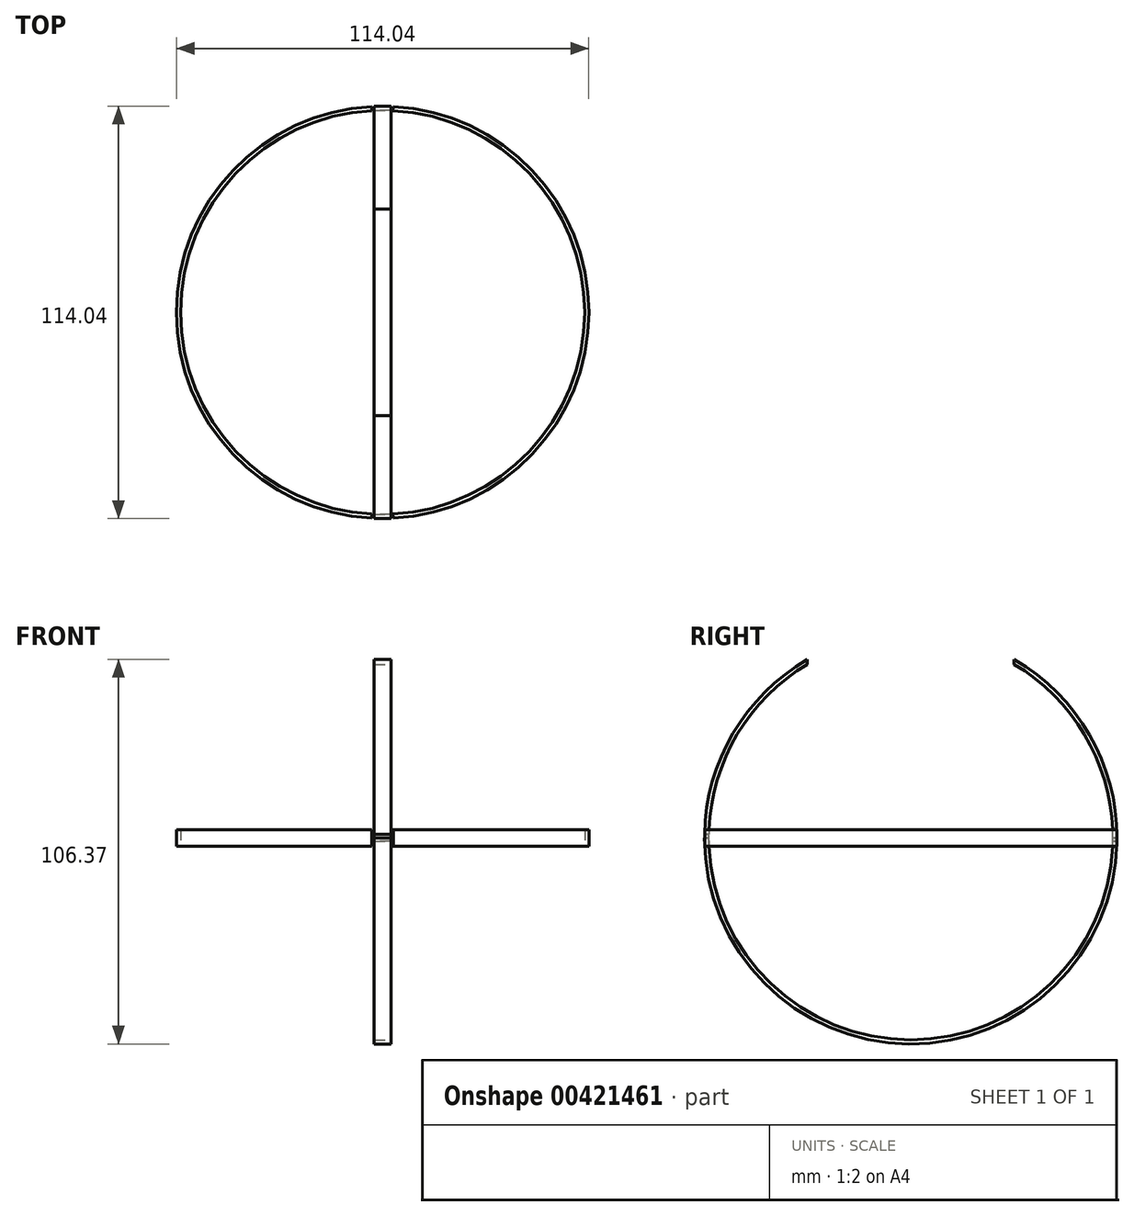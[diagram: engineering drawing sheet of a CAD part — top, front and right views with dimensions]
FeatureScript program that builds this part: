
annotation { "Feature Type Name" : "Feature", "Feature Type Description" : "" }
export const myFeature = defineFeature(function(context is Context, id is Id, definition is map)
    precondition{}
    {
        {
            var Q0;
            Q0=qCreatedBy(makeId("Front.planeOp"),FACE);
            var sketch = newSketch(context, id + "F0", { "sketchPlane" : qUnion([Q0])});
            skLineSegment(sketch, "E0", {"start": v(0, 0) * mm, "end": v(55.88, 0) * mm});
            skLineSegment(sketch, "E1", {"start": v(55.88, 0) * mm, "end": v(55.88, 2.29) * mm});
            skLineSegment(sketch, "E2", {"start": v(55.88, 2.29) * mm, "end": v(57.02, 2.29) * mm});
            skLineSegment(sketch, "E3", {"start": v(57.02, 2.29) * mm, "end": v(57.02, -2.29) * mm});
            skLineSegment(sketch, "E4", {"start": v(57.02, -2.29) * mm, "end": v(55.88, -2.29) * mm});
            skLineSegment(sketch, "E5", {"start": v(55.88, -2.29) * mm, "end": v(55.88, 0) * mm});
            skLineSegment(sketch, "E6", {"start": v(0, 0) * mm, "end": v(0, 55.88) * mm});
            skLineSegment(sketch, "E7", {"start": v(0, 55.88) * mm, "end": v(2.29, 55.88) * mm});
            skLineSegment(sketch, "E8", {"start": v(2.29, 55.88) * mm, "end": v(2.29, 57.02) * mm});
            skLineSegment(sketch, "E9", {"start": v(2.29, 57.02) * mm, "end": v(-2.29, 57.02) * mm});
            skLineSegment(sketch, "E10", {"start": v(-2.29, 57.02) * mm, "end": v(-2.29, 55.88) * mm});
            skLineSegment(sketch, "E11", {"start": v(0, 55.88) * mm, "end": v(-2.29, 55.88) * mm});
            skLineSegment(sketch, "E12.MirrorCS", {"start": v(-55.88, 0) * mm, "end": v(-55.88, 2.29) * mm});
            skLineSegment(sketch, "E13.MirrorCS", {"start": v(0, 0) * mm, "end": v(-55.88, 0) * mm});
            skLineSegment(sketch, "E14.MirrorCS", {"start": v(-55.88, -2.29) * mm, "end": v(-55.88, 0) * mm});
            skLineSegment(sketch, "E15.MirrorCS", {"start": v(-57.02, -2.29) * mm, "end": v(-55.88, -2.29) * mm});
            skLineSegment(sketch, "E16.MirrorCS", {"start": v(-57.02, 2.29) * mm, "end": v(-57.02, -2.29) * mm});
            skLineSegment(sketch, "E17.MirrorCS", {"start": v(-55.88, 2.29) * mm, "end": v(-57.02, 2.29) * mm});
            skLineSegment(sketch, "E18.MirrorCS", {"start": v(0, 0) * mm, "end": v(0, -55.88) * mm});
            skLineSegment(sketch, "E19.MirrorCS", {"start": v(2.29, -57.02) * mm, "end": v(-2.29, -57.02) * mm});
            skLineSegment(sketch, "E20.MirrorCS", {"start": v(-2.29, -57.02) * mm, "end": v(-2.29, -55.88) * mm});
            skLineSegment(sketch, "E21.MirrorCS", {"start": v(0, -55.88) * mm, "end": v(-2.29, -55.88) * mm});
            skLineSegment(sketch, "E22.MirrorCS", {"start": v(0, -55.88) * mm, "end": v(2.29, -55.88) * mm});
            skLineSegment(sketch, "E23.MirrorCS", {"start": v(2.29, -55.88) * mm, "end": v(2.29, -57.02) * mm});
            skSolve(sketch);
        }
        {
            var Q0;
            Q0=makeQuery(id+"F0.imprint","IMPRINT",FACE,{"disambiguationData":[TD([[makeQuery(id+"F0.imprint","IMPRINT",EDGE,{"derivedFrom":sQuery(id+"F0.wireOp",EDGE,"E19.MirrorCS")}),-1.0]])]});
            var Q1;
            Q1=makeQuery(id+"F0.imprint","IMPRINT",FACE,{"disambiguationData":[TD([[makeQuery(id+"F0.imprint","IMPRINT",EDGE,{"derivedFrom":sQuery(id+"F0.wireOp",EDGE,"E7")}),1.0]])]});
            var Q2;
            Q2=sQuery(id+"F0.wireOp",EDGE,"E13.MirrorCS");
            revolve(context, id + "F1", {"entities" : qUnion([Q0, Q1]), "axis" : qUnion([Q2]), "revolveType" : RevolveType.TWO_DIRECTIONS, "angle" : 90 * degree, "angleBack" : 271 * degree});
        }
        {
            var Q0;
            Q0=makeQuery(id+"F0.imprint","IMPRINT",FACE,{"disambiguationData":[TD([[makeQuery(id+"F0.imprint","IMPRINT",EDGE,{"derivedFrom":sQuery(id+"F0.wireOp",EDGE,"E12.MirrorCS")}),1.0]])]});
            var Q1;
            Q1=makeQuery(id+"F0.imprint","IMPRINT",FACE,{"disambiguationData":[TD([[makeQuery(id+"F0.imprint","IMPRINT",EDGE,{"derivedFrom":sQuery(id+"F0.wireOp",EDGE,"E1")}),-1.0]])]});
            var Q2;
            Q2=sQuery(id+"F0.wireOp",EDGE,"E6");
            revolve(context, id + "F2", {"entities" : qUnion([Q0, Q1]), "axis" : qUnion([Q2]), "revolveType" : RevolveType.TWO_DIRECTIONS, "angle" : 87 * degree, "angleBack" : 273 * degree});
        }
        {
            var Q0;
            Q0=qCreatedBy(makeId("Right.planeOp"),FACE);
            var sketch = newSketch(context, id + "F3", { "sketchPlane" : qUnion([Q0])});
            skLineSegment(sketch, "E24", {"start": v(0, 0) * mm, "end": v(0, 60.96) * mm});
            skLineSegment(sketch, "E25", {"start": v(0, 60.96) * mm, "end": v(-28.57, 60.96) * mm});
            skLineSegment(sketch, "E26", {"start": v(-28.57, 60.96) * mm, "end": v(-28.57, 41.91) * mm});
            skLineSegment(sketch, "E27", {"start": v(-28.57, 41.91) * mm, "end": v(28.58, 41.91) * mm});
            skLineSegment(sketch, "E28", {"start": v(28.58, 41.91) * mm, "end": v(28.58, 60.96) * mm});
            skLineSegment(sketch, "E29", {"start": v(28.58, 60.96) * mm, "end": v(0, 60.96) * mm});
            skSolve(sketch);
        }
        {
            var Q0;
            Q0 = qSketchRegion(id + "F3", true);
            extrude(context, id + "F4", {"entities" : qUnion([Q0]), "operationType" : NewBodyOperationType.REMOVE, "endBound" : BoundingType.SYMMETRIC, "oppositeDirection" : true, "depth" : 25.4 * mm});
        }
    });
